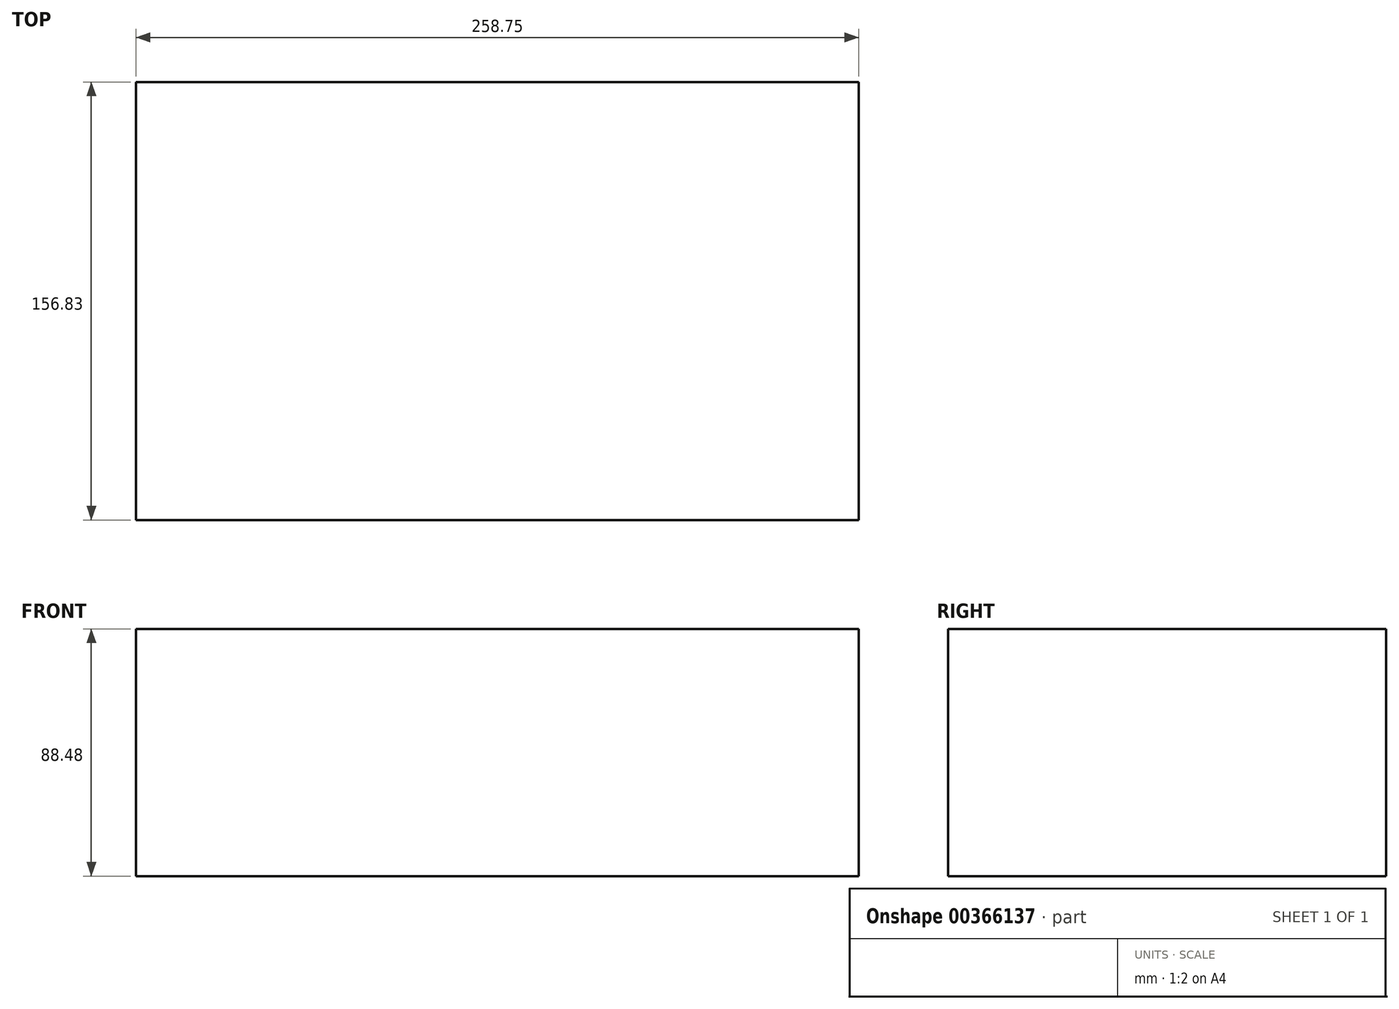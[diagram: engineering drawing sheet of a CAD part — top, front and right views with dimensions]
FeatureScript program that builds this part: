
annotation { "Feature Type Name" : "Feature", "Feature Type Description" : "" }
export const myFeature = defineFeature(function(context is Context, id is Id, definition is map)
    precondition{}
    {
        {
            var Q0;
            Q0=qCreatedBy(makeId("Top.planeOp"),FACE);
            var sketch = newSketch(context, id + "F0", { "sketchPlane" : qUnion([Q0])});
            skLineSegment(sketch, "E0.bottom", {"start": v(-82.53, 44.8) * mm, "end": v(129.8, 44.8) * mm});
            skLineSegment(sketch, "E0.top", {"start": v(-82.53, -112.03) * mm, "end": v(129.8, -112.03) * mm});
            skLineSegment(sketch, "E0.left", {"start": v(-82.53, 44.8) * mm, "end": v(-82.53, -112.03) * mm});
            skLineSegment(sketch, "E0.right", {"start": v(129.8, 44.8) * mm, "end": v(129.8, -112.03) * mm});
            skSolve(sketch);
        }
        {
            var Q0;
            Q0 = qSketchRegion(id + "F0", true);
            extrude(context, id + "F1", {"entities" : qUnion([Q0]), "depth" : 88.48 * mm});
        }
        {
            var Q0;
            Q0=makeQuery(id+"F1.opExtrude","SWEPT_FACE",FACE,{"disambiguationData":[OSD([sQuery(id+"F0.wireOp",EDGE,"E0.right")])]});
            extrude(context, id + "F2", {"entities" : qUnion([Q0]), "operationType" : NewBodyOperationType.ADD, "depth" : 46.42 * mm});
        }
    });
